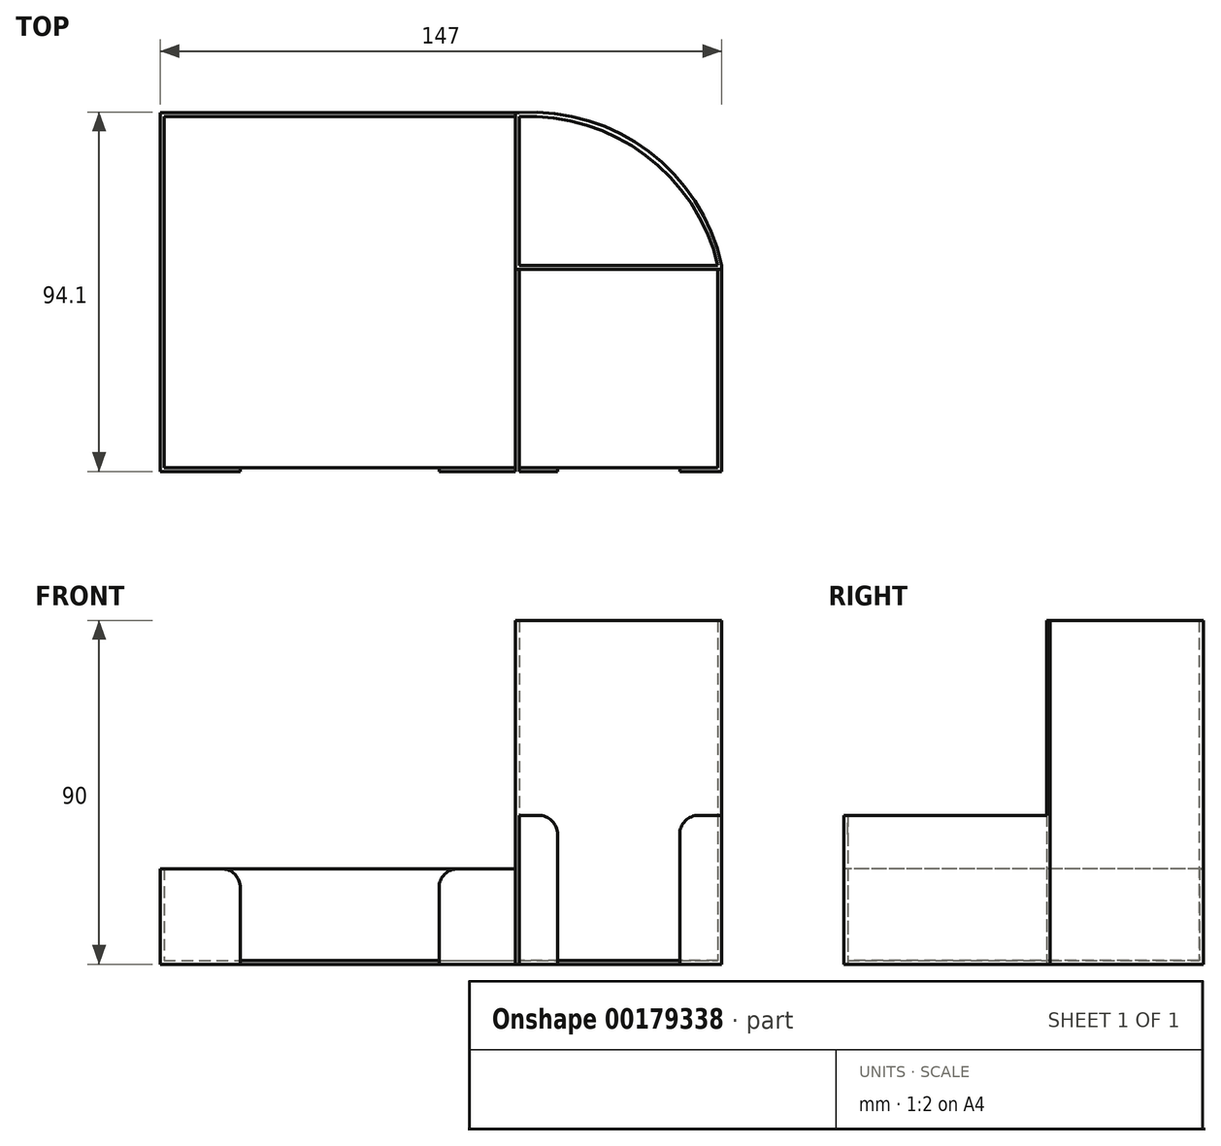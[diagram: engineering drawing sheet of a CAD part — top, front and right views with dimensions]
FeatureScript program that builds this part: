
annotation { "Feature Type Name" : "Feature", "Feature Type Description" : "" }
export const myFeature = defineFeature(function(context is Context, id is Id, definition is map)
    precondition{}
    {
        {
            var Q0;
            Q0=qCreatedBy(makeId("Top.planeOp"),FACE);
            var sketch = newSketch(context, id + "F0", { "sketchPlane" : qUnion([Q0])});
            skLineSegment(sketch, "E0.bottom", {"start": v(-87.73, 55.21) * mm, "end": v(4.27, 55.21) * mm});
            skLineSegment(sketch, "E0.top", {"start": v(-87.73, -36.79) * mm, "end": v(4.27, -36.79) * mm});
            skLineSegment(sketch, "E0.left", {"start": v(-87.73, 55.21) * mm, "end": v(-87.73, -36.79) * mm});
            skLineSegment(sketch, "E0.right", {"start": v(4.27, 55.21) * mm, "end": v(4.27, -36.79) * mm});
            skLineSegment(sketch, "E1.bottom", {"start": v(-88.73, 56.21) * mm, "end": v(5.27, 56.21) * mm});
            skLineSegment(sketch, "E1.top", {"start": v(-88.73, -37.79) * mm, "end": v(5.27, -37.79) * mm});
            skLineSegment(sketch, "E1.left", {"start": v(-88.73, 56.21) * mm, "end": v(-88.73, -37.79) * mm});
            skLineSegment(sketch, "E1.right", {"start": v(5.27, 56.21) * mm, "end": v(5.27, -37.79) * mm});
            skLineSegment(sketch, "E2.bottom", {"start": v(5.27, -36.79) * mm, "end": v(57.27, -36.79) * mm});
            skLineSegment(sketch, "E2.top", {"start": v(5.27, 15.21) * mm, "end": v(57.27, 15.21) * mm});
            skLineSegment(sketch, "E2.left", {"start": v(5.27, -36.79) * mm, "end": v(5.27, 15.21) * mm});
            skLineSegment(sketch, "E2.right", {"start": v(57.27, -36.79) * mm, "end": v(57.27, 15.21) * mm});
            skLineSegment(sketch, "E3", {"start": v(5.27, -37.79) * mm, "end": v(58.27, -37.79) * mm});
            skLineSegment(sketch, "E4", {"start": v(58.27, -37.79) * mm, "end": v(58.27, 16.21) * mm});
            skLineSegment(sketch, "E5", {"start": v(58.27, 16.21) * mm, "end": v(5.27, 16.21) * mm});
            skArc(sketch, "E6", {"start": v(58.27, 16.21) * mm, "mid": v(39.16, 46) * mm, "end": v(5.27, 56.21) * mm});
            skPoint(sketch, "E7", {"position": v(5.27, 55.12) * mm});
            skPoint(sketch, "E8", {"position": v(57.27, 16.21) * mm});
            skArc(sketch, "E9", {"start": v(57.27, 16.21) * mm, "mid": v(38.3, 45.05) * mm, "end": v(5.27, 55.12) * mm});
            skLineSegment(sketch, "E10", {"start": v(57.27, 15.21) * mm, "end": v(58.27, 15.21) * mm});
            skLineSegment(sketch, "E11", {"start": v(5.27, 15.21) * mm, "end": v(4.27, 15.21) * mm});
            skLineSegment(sketch, "E12", {"start": v(4.27, 55.21) * mm, "end": v(4.27, 56.21) * mm});
            skLineSegment(sketch, "E13", {"start": v(4.27, -36.79) * mm, "end": v(4.27, -37.79) * mm});
            skLineSegment(sketch, "E14", {"start": v(-67.73, -36.79) * mm, "end": v(-67.73, -37.79) * mm});
            skLineSegment(sketch, "E15", {"start": v(-15.73, -36.79) * mm, "end": v(-15.73, -37.79) * mm});
            skLineSegment(sketch, "E16", {"start": v(15.27, -36.79) * mm, "end": v(15.27, -37.79) * mm});
            skLineSegment(sketch, "E17", {"start": v(47.27, -36.79) * mm, "end": v(47.27, -37.79) * mm});
            skSolve(sketch);
        }
        {
            var Q0;
            {var subQ0=sQuery(id+"F0.wireOp",EDGE,"E6");Q0=makeQuery(id+"F0.imprint","IMPRINT",FACE,{"disambiguationData":[TD([[makeQuery(id+"F0.imprint","IMPRINT",EDGE,{"derivedFrom":subQ0}),1.0]])]});}
            var Q1;
            {var subQ5=sQuery(id+"F0.wireOp",EDGE,"E2.top");Q1=makeQuery(id+"F0.imprint","IMPRINT",FACE,{"disambiguationData":[TD([[makeQuery(id+"F0.imprint","IMPRINT",EDGE,{"derivedFrom":subQ5}),1.0]])]});}
            var Q2;
            {var subQ7=sQuery(id+"F0.wireOp",EDGE,"E11");Q2=makeQuery(id+"F0.imprint","IMPRINT",FACE,{"disambiguationData":[TD([[makeQuery(id+"F0.imprint","IMPRINT",EDGE,{"derivedFrom":subQ7}),-1.0]])]});}
            extrude(context, id + "F1", {"entities" : qUnion([Q0, Q1, Q2]), "depth" : 90 * mm});
        }
        {
            var Q0;
            {var subQ4=sQuery(id+"F0.wireOp",EDGE,"E2.right");Q0=makeQuery(id+"F0.imprint","IMPRINT",FACE,{"disambiguationData":[TD([[makeQuery(id+"F0.imprint","IMPRINT",EDGE,{"derivedFrom":subQ4}),-1.0]])]});}
            var Q1;
            {var subQ3=sQuery(id+"F0.wireOp",EDGE,"E2.left");Q1=makeQuery(id+"F0.imprint","IMPRINT",FACE,{"disambiguationData":[TD([[makeQuery(id+"F0.imprint","IMPRINT",EDGE,{"derivedFrom":subQ3}),1.0]])]});}
            var Q2;
            {var subQ5=sQuery(id+"F0.wireOp",EDGE,"E16");Q2=makeQuery(id+"F0.imprint","IMPRINT",FACE,{"disambiguationData":[TD([[makeQuery(id+"F0.imprint","IMPRINT",EDGE,{"derivedFrom":subQ5}),-1.0]])]});}
            extrude(context, id + "F2", {"entities" : qUnion([Q0, Q1, Q2]), "operationType" : NewBodyOperationType.ADD, "depth" : 39 * mm});
        }
        {
            var Q0;
            Q0=makeQuery(id+"F0.imprint","IMPRINT",FACE,{"disambiguationData":[TD([[makeQuery(id+"F0.imprint","IMPRINT",EDGE,{"derivedFrom":sQuery(id+"F0.wireOp",EDGE,"E0.bottom")}),1.0]])]});
            var Q1;
            {var subQ0=sQuery(id+"F0.wireOp",EDGE,"E13");Q1=makeQuery(id+"F0.imprint","IMPRINT",FACE,{"disambiguationData":[TD([[makeQuery(id+"F0.imprint","IMPRINT",EDGE,{"derivedFrom":subQ0}),-1.0]])]});}
            extrude(context, id + "F3", {"entities" : qUnion([Q0, Q1]), "operationType" : NewBodyOperationType.ADD, "depth" : 25 * mm});
        }
        {
            var Q0;
            {var subQ6=sQuery(id+"F0.wireOp",EDGE,"E0.bottom");Q0=makeQuery(id+"F0.imprint","IMPRINT",FACE,{"disambiguationData":[TD([[makeQuery(id+"F0.imprint","IMPRINT",EDGE,{"derivedFrom":subQ6}),-1.0]])]});}
            var Q1;
            Q1=makeQuery(id+"F0.imprint","IMPRINT",FACE,{"disambiguationData":[TD([[makeQuery(id+"F0.imprint","IMPRINT",EDGE,{"derivedFrom":sQuery(id+"F0.wireOp",EDGE,"E2.top")}),-1.0]])]});
            var Q2;
            {var subQ3=sQuery(id+"F0.wireOp",EDGE,"E9");Q2=makeQuery(id+"F0.imprint","IMPRINT",FACE,{"disambiguationData":[TD([[makeQuery(id+"F0.imprint","IMPRINT",EDGE,{"derivedFrom":subQ3}),1.0]])]});}
            extrude(context, id + "F4", {"entities" : qUnion([Q0, Q1, Q2]), "operationType" : NewBodyOperationType.ADD, "depth" : 1 * mm});
        }
        {
            var Q0;
            Q0=makeQuery(id+"F3.opExtrude","CAP_EDGE",EDGE,{"disambiguationData":[OSD([sQuery(id+"F0.wireOp",EDGE,"E14")])],"isStart":false});
            fillet(context, id + "F5", {"entities" : qUnion([Q0]), "radius" : 5 * mm, "tangentPropagation" : true, "allowEdgeOverflow" : false});
        }
        {
            var Q0;
            Q0=makeQuery(id+"F3.opExtrude","CAP_EDGE",EDGE,{"disambiguationData":[OSD([sQuery(id+"F0.wireOp",EDGE,"E15")])],"isStart":false});
            fillet(context, id + "F6", {"entities" : qUnion([Q0]), "radius" : 5 * mm, "tangentPropagation" : true, "allowEdgeOverflow" : false});
        }
        {
            var Q0;
            Q0=makeQuery(id+"F2.opExtrude","CAP_EDGE",EDGE,{"disambiguationData":[OSD([sQuery(id+"F0.wireOp",EDGE,"E16")])],"isStart":false});
            fillet(context, id + "F7", {"entities" : qUnion([Q0]), "radius" : 5 * mm, "tangentPropagation" : true, "allowEdgeOverflow" : false});
        }
        {
            var Q0;
            Q0=makeQuery(id+"F2.opExtrude","CAP_EDGE",EDGE,{"disambiguationData":[OSD([sQuery(id+"F0.wireOp",EDGE,"E17")])],"isStart":false});
            fillet(context, id + "F8", {"entities" : qUnion([Q0]), "radius" : 5 * mm, "tangentPropagation" : true, "allowEdgeOverflow" : false});
        }
    });
